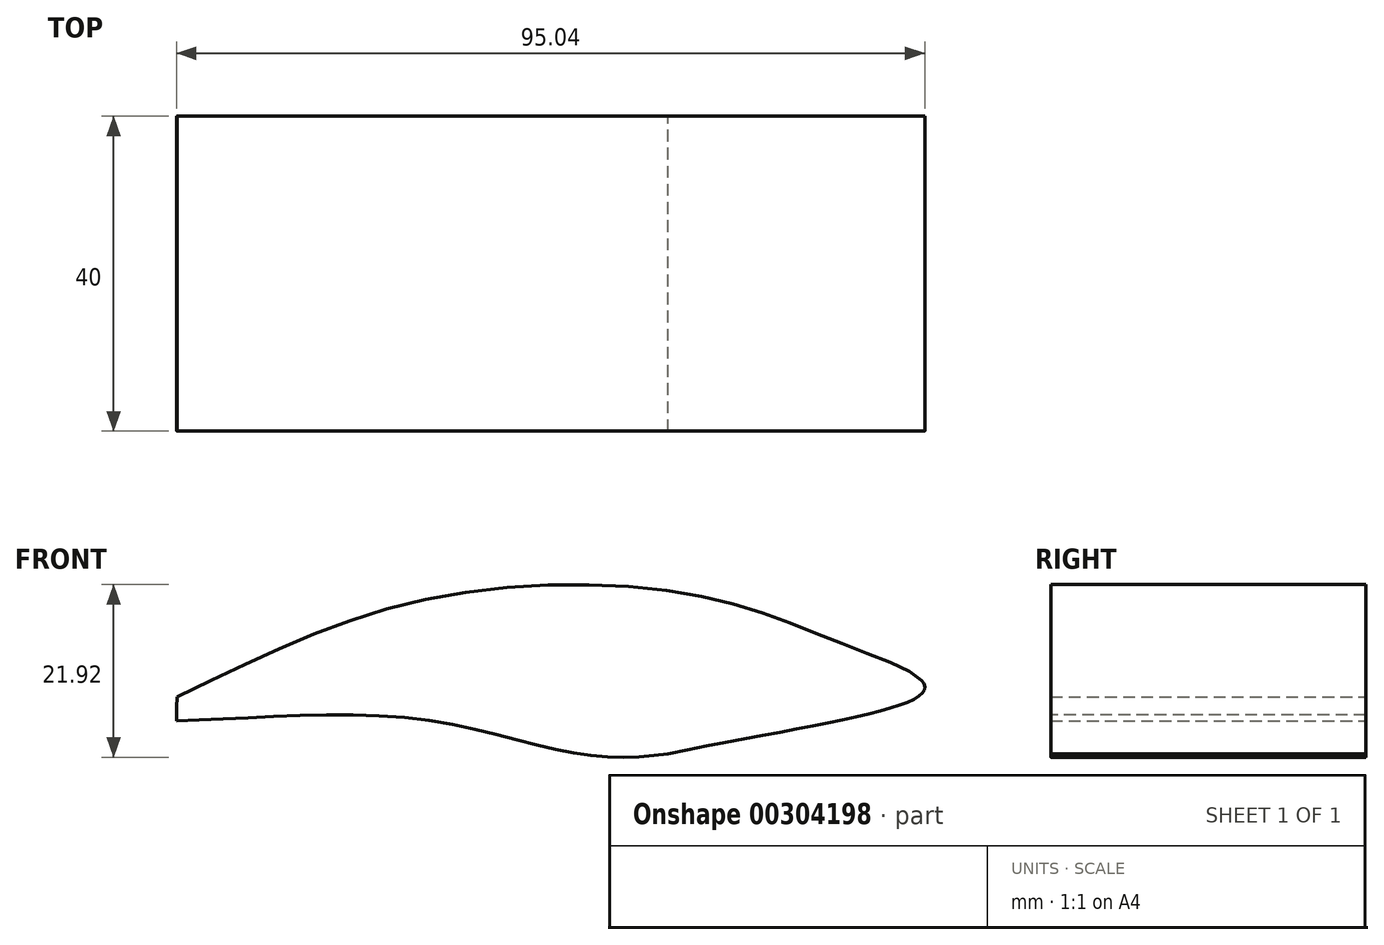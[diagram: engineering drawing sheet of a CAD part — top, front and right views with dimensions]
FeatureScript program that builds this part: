
annotation { "Feature Type Name" : "Feature", "Feature Type Description" : "" }
export const myFeature = defineFeature(function(context is Context, id is Id, definition is map)
    precondition{}
    {
        {
            var Q0;
            Q0=qCreatedBy(makeId("Front.planeOp"),FACE);
            var sketch = newSketch(context, id + "F0", { "sketchPlane" : qUnion([Q0])});
            skFitSpline(sketch, "E0", {"points": [v(0.05, 3.02) * mm, v(0, 0) * mm], "startDerivative": vector(-0.16, -5.6) * mm, "endDerivative": vector(-0.16, -5.6) * mm});
            skFitSpline(sketch, "E1", {"points": [v(62.41, -4.18) * mm, v(50.9, -4.18) * mm, v(30.05, 0.3) * mm, v(0, 0) * mm], "startDerivative": vector(-40.42, -6.02) * mm, "endDerivative": vector(-63.17, -1.46) * mm});
            skLineSegment(sketch, "E2", {"start": v(94.63, 5.15) * mm, "end": v(91.97, 5.1) * mm});
            skFitSpline(sketch, "E3.trimOffspring", {"points": [v(0.05, 3.02) * mm, v(30.52, 15.16) * mm, v(65.92, 15.95) * mm, v(84.9, 9.66) * mm, v(94.63, 5.15) * mm, v(94.63, 3.4) * mm, v(62.41, -4.18) * mm], "startDerivative": vector(135.72, 65.1) * mm, "endDerivative": vector(-214.94, -43.13) * mm});
            skFitSpline(sketch, "E4.0", {"points": [v(62.12, -2.2) * mm, v(61.31, -2.32) * mm, v(59.66, -2.53) * mm, v(57.03, -2.67) * mm, v(54.72, -2.6) * mm, v(52.79, -2.43) * mm, v(51.3, -2.23) * mm, v(49.75, -1.95) * mm, v(47.6, -1.48) * mm, v(44.71, -0.75) * mm, v(40.98, 0.24) * mm, v(37.62, 1.04) * mm, v(34.78, 1.61) * mm, v(32.58, 2) * mm, v(30.29, 2.3) * mm, v(27.14, 2.6) * mm, v(23.1, 2.78) * mm, v(18.17, 2.77) * mm, v(13.27, 2.6) * mm, v(6.92, 2.3) * mm, v(2.54, 2.06) * mm, v(-0.05, 2) * mm]});
            skLineSegment(sketch, "E5", {"start": v(62.12, -2.2) * mm, "end": v(90.7, 3.16) * mm});
            skFitSpline(sketch, "E6", {"points": [v(90.7, 3.16) * mm, v(91.97, 5.1) * mm], "startDerivative": vector(1.28, 1.94) * mm, "endDerivative": vector(1.28, 1.94) * mm});
            skSolve(sketch);
        }
        {
            var Q0;
            Q0 = qSketchRegion(id + "F0", true);
            extrude(context, id + "F1", {"entities" : qUnion([Q0]), "depth" : 40 * mm});
        }
    });
